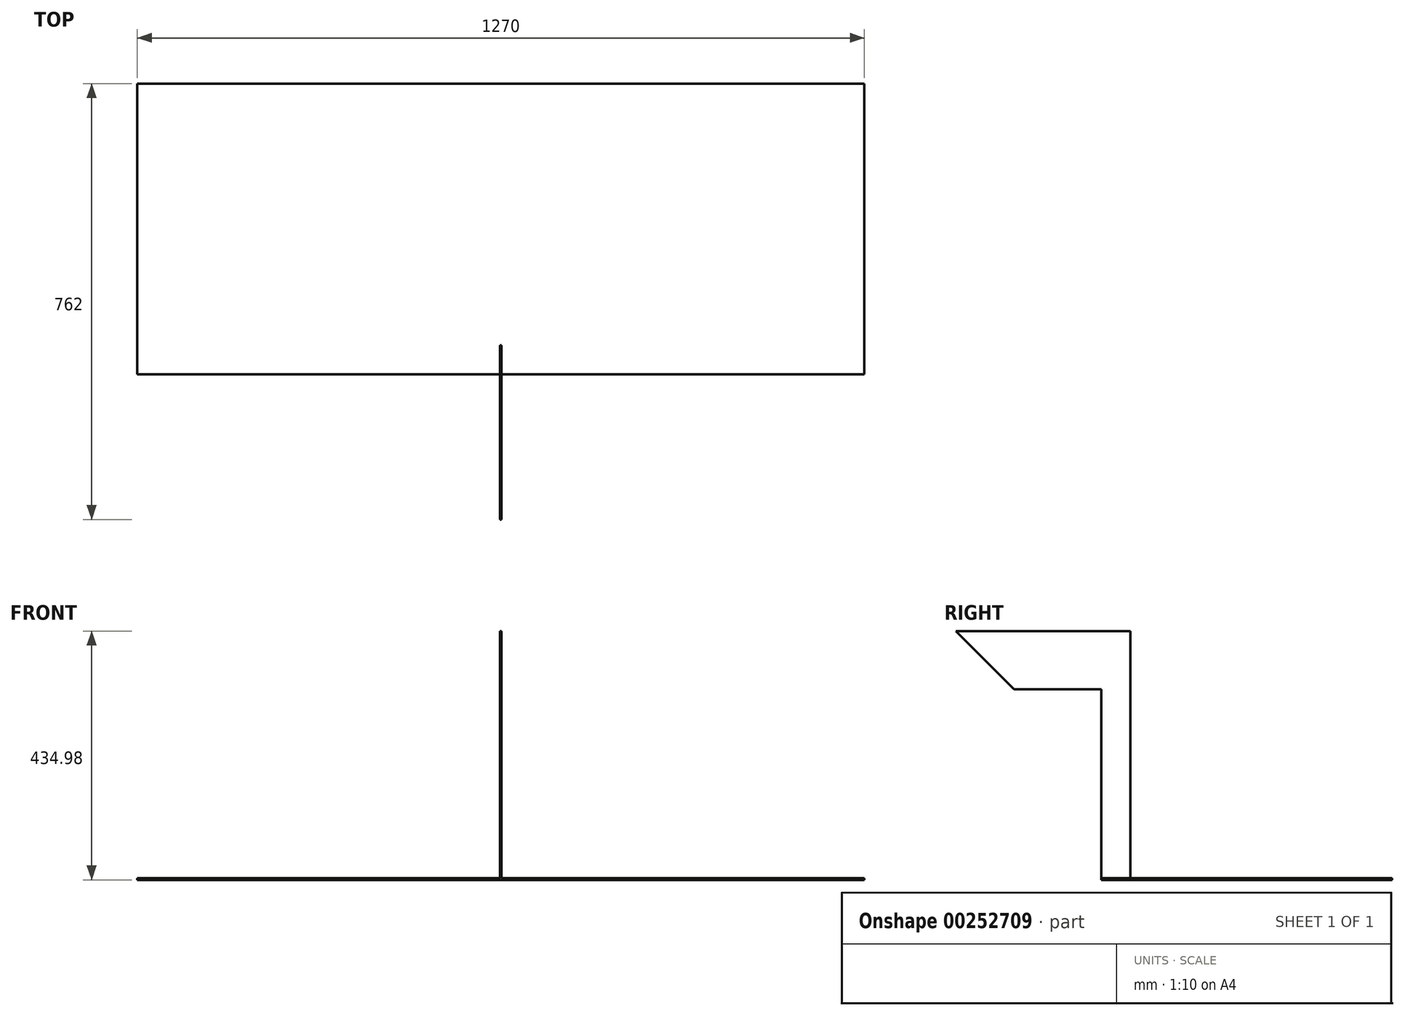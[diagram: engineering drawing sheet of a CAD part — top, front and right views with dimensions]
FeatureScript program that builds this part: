
annotation { "Feature Type Name" : "Feature", "Feature Type Description" : "" }
export const myFeature = defineFeature(function(context is Context, id is Id, definition is map)
    precondition{}
    {
        {
            var Q0;
            Q0=qCreatedBy(makeId("Top.planeOp"),FACE);
            var sketch = newSketch(context, id + "F0", { "sketchPlane" : qUnion([Q0])});
            skLineSegment(sketch, "E0.bottom", {"start": v(-635, 254) * mm, "end": v(635, 254) * mm});
            skLineSegment(sketch, "E0.top", {"start": v(-635, -254) * mm, "end": v(635, -254) * mm});
            skLineSegment(sketch, "E0.left", {"start": v(-635, 254) * mm, "end": v(-635, -254) * mm});
            skLineSegment(sketch, "E0.right", {"start": v(635, 254) * mm, "end": v(635, -254) * mm});
            skPoint(sketch, "E0.middle", {"position": v(0, 0) * mm});
            skSolve(sketch);
        }
        {
            var Q0;
            Q0 = qSketchRegion(id + "F0", true);
            extrude(context, id + "F1", {"entities" : qUnion([Q0]), "depth" : 3.17 * mm});
        }
        {
            var Q0;
            Q0=qCreatedBy(makeId("Right.planeOp"),FACE);
            var sketch = newSketch(context, id + "F2", { "sketchPlane" : qUnion([Q0])});
            skLineSegment(sketch, "E1", {"start": v(-254, 3.18) * mm, "end": v(-254, 333.38) * mm});
            skLineSegment(sketch, "E2", {"start": v(-254, 333.38) * mm, "end": v(-406.4, 333.38) * mm});
            skLineSegment(sketch, "E3", {"start": v(-406.4, 333.38) * mm, "end": v(-508, 434.98) * mm});
            skLineSegment(sketch, "E4", {"start": v(-508, 434.98) * mm, "end": v(-203.2, 434.98) * mm});
            skLineSegment(sketch, "E5", {"start": v(-203.2, 434.98) * mm, "end": v(-203.2, 3.18) * mm});
            skLineSegment(sketch, "E6", {"start": v(-203.2, 3.18) * mm, "end": v(-254, 3.18) * mm});
            skSolve(sketch);
        }
        {
            var Q0;
            Q0 = qSketchRegion(id + "F2", true);
            extrude(context, id + "F3", {"entities" : qUnion([Q0]), "operationType" : NewBodyOperationType.ADD, "endBound" : BoundingType.SYMMETRIC, "depth" : 2.54 * mm});
        }
    });
